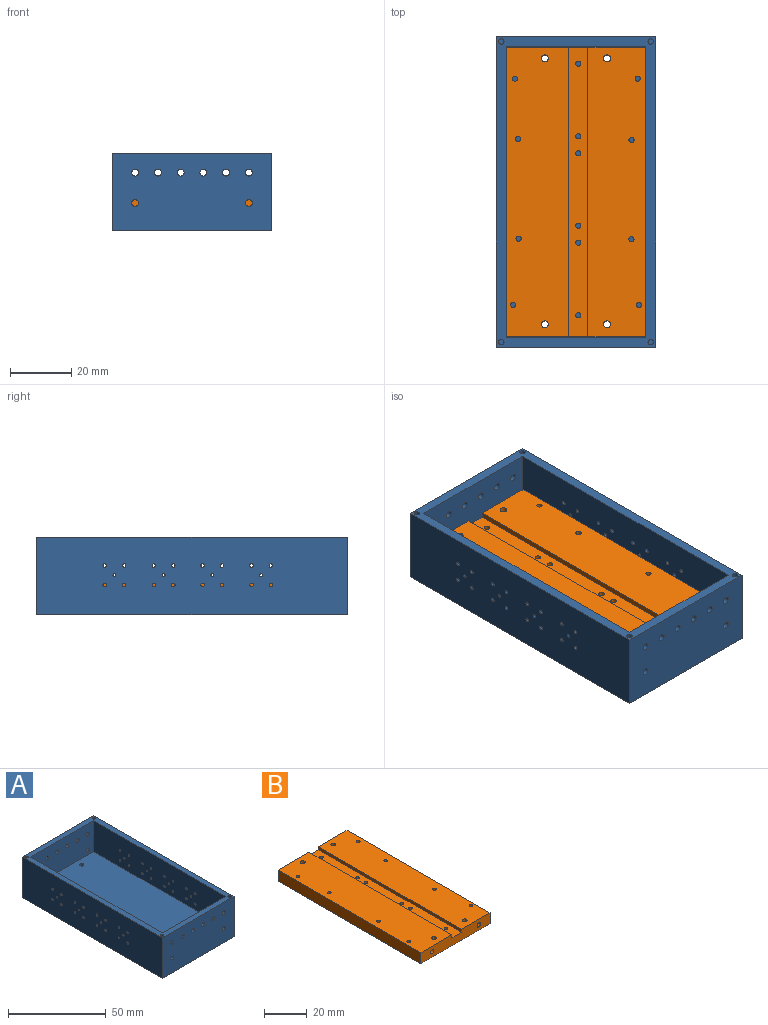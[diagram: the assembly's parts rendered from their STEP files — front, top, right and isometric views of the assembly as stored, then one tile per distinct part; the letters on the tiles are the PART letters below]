
ASSEMBLY  parts=2 mates=1
PART A: 79 faces, bbox 52.1x101.6x25.4 mm
  f0: plane 95.3x45.77mm, normal (0,0,1), area 4345.9mm2, adj f3,f5,f9,f10,f75,f76,f77,f78
  f1: plane 101.6x52.07mm, normal (0,0,-1), area 5274.3mm2, adj f2,f4,f7,f8,f75,f76,f77,f78
  f2: plane 52.07x25.4mm, normal (0,1,0), area 1290.5mm2, adj f1,f6,f7,f8,f11,f12,f13,f14
  f3: plane 45.77x19.46mm, normal (0,-1,0), area 858.4mm2, adj f0,f6,f9,f10,f11,f12,f13,f14
  f4: plane 52.07x25.4mm, normal (0,-1,0), area 1290.5mm2, adj f1,f6,f7,f8,f17,f18,f19,f20
  f5: plane 45.77x19.46mm, normal (0,1,0), area 858.4mm2, adj f0,f6,f9,f10,f17,f18,f19,f20
  f6: plane 101.6x52.07mm, normal (0,0,1), area 918.4mm2, adj f2,f3,f4,f5,f7,f8,f9,f10
  f7: plane 101.6x25.4mm, normal (-1,0,0), area 2560mm2, adj f1,f2,f4,f6,f43,f44,f45,f46
  f8: plane 101.6x25.4mm, normal (1,0,0), area 2560mm2, adj f1,f2,f4,f6,f23,f24,f25,f26
  f9: plane 95.3x19.46mm, normal (1,0,0), area 1833.6mm2, adj f0,f3,f5,f6,f43,f44,f45,f46
  f10: plane 95.3x19.46mm, normal (-1,0,0), area 1833.6mm2, adj f0,f3,f5,f6,f23,f24,f25,f26
  f11: cylinder r=1.13mm len=3.15mm, axis (0,1,0), area 22.4mm2, adj f2,f3
  f12: cylinder r=1.13mm len=3.15mm, axis (0,1,0), area 22.4mm2, adj f2,f3
  f13: cylinder r=1.13mm len=3.15mm, axis (0,1,0), area 22.4mm2, adj f2,f3
  f14: cylinder r=1.13mm len=3.15mm, axis (0,1,0), area 22.4mm2, adj f2,f3
  f15: cylinder r=1.13mm len=3.15mm, axis (0,1,0), area 22.4mm2, adj f2,f3
  f16: cylinder r=1.13mm len=3.15mm, axis (0,1,0), area 22.4mm2, adj f2,f3
  f17: cylinder r=1.13mm len=3.15mm, axis (0,-1,0), area 22.4mm2, adj f4,f5
  f18: cylinder r=1.13mm len=3.15mm, axis (0,-1,0), area 22.4mm2, adj f4,f5
  f19: cylinder r=1.13mm len=3.15mm, axis (0,-1,0), area 22.4mm2, adj f4,f5
  f20: cylinder r=1.13mm len=3.15mm, axis (0,-1,0), area 22.4mm2, adj f4,f5
  f21: cylinder r=1.13mm len=3.15mm, axis (0,-1,0), area 22.4mm2, adj f4,f5
  f22: cylinder r=1.13mm len=3.15mm, axis (0,-1,0), area 22.4mm2, adj f4,f5
  f23: cylinder r=0.59mm len=3.15mm, axis (1,0,0), area 11.7mm2, adj f8,f10
  f24: cylinder r=0.5mm len=3.15mm, axis (1,0,0), area 9.8mm2, adj f8,f10
  f25: cylinder r=0.59mm len=3.15mm, axis (1,0,0), area 11.7mm2, adj f8,f10
  f26: cylinder r=0.59mm len=3.15mm, axis (1,0,0), area 11.7mm2, adj f8,f10
  f27: cylinder r=0.59mm len=3.15mm, axis (1,0,0), area 11.7mm2, adj f8,f10
  f28: cylinder r=0.5mm len=3.15mm, axis (1,0,0), area 9.8mm2, adj f8,f10
  f29: cylinder r=0.59mm len=3.15mm, axis (1,0,0), area 11.7mm2, adj f8,f10
  f30: cylinder r=0.59mm len=3.15mm, axis (1,0,0), area 11.7mm2, adj f8,f10
  f31: cylinder r=0.59mm len=3.15mm, axis (1,0,0), area 11.7mm2, adj f8,f10
  f32: cylinder r=0.59mm len=3.15mm, axis (1,0,0), area 11.7mm2, adj f8,f10
  f33: cylinder r=0.59mm len=3.15mm, axis (1,0,0), area 11.7mm2, adj f8,f10
  f34: cylinder r=0.59mm len=3.15mm, axis (1,0,0), area 11.7mm2, adj f8,f10
  f35: cylinder r=0.59mm len=3.15mm, axis (1,0,0), area 11.7mm2, adj f8,f10
  f36: cylinder r=0.59mm len=3.15mm, axis (1,0,0), area 11.7mm2, adj f8,f10
  f37: cylinder r=0.5mm len=3.15mm, axis (1,0,0), area 9.8mm2, adj f8,f10
  f38: cylinder r=0.59mm len=3.15mm, axis (1,0,0), area 11.7mm2, adj f8,f10
  f39: cylinder r=0.5mm len=3.15mm, axis (1,0,0), area 9.8mm2, adj f8,f10
  f40: cylinder r=0.59mm len=3.15mm, axis (1,0,0), area 11.7mm2, adj f8,f10
  f41: cylinder r=0.59mm len=3.15mm, axis (1,0,0), area 11.7mm2, adj f8,f10
  f42: cylinder r=0.59mm len=3.15mm, axis (1,0,0), area 11.7mm2, adj f8,f10
  f43: cylinder r=0.59mm len=3.15mm, axis (-1,0,0), area 11.7mm2, adj f7,f9
  f44: cylinder r=0.5mm len=3.15mm, axis (-1,0,0), area 9.8mm2, adj f7,f9
  f45: cylinder r=0.59mm len=3.15mm, axis (-1,0,0), area 11.7mm2, adj f7,f9
  f46: cylinder r=0.59mm len=3.15mm, axis (-1,0,0), area 11.7mm2, adj f7,f9
  f47: cylinder r=0.59mm len=3.15mm, axis (-1,0,0), area 11.7mm2, adj f7,f9
  f48: cylinder r=0.5mm len=3.15mm, axis (-1,0,0), area 9.8mm2, adj f7,f9
  f49: cylinder r=0.59mm len=3.15mm, axis (-1,0,0), area 11.7mm2, adj f7,f9
  f50: cylinder r=0.59mm len=3.15mm, axis (-1,0,0), area 11.7mm2, adj f7,f9
  f51: cylinder r=0.59mm len=3.15mm, axis (-1,0,0), area 11.7mm2, adj f7,f9
  f52: cylinder r=0.59mm len=3.15mm, axis (-1,0,0), area 11.7mm2, adj f7,f9
  f53: cylinder r=0.59mm len=3.15mm, axis (-1,0,0), area 11.7mm2, adj f7,f9
  f54: cylinder r=0.59mm len=3.15mm, axis (-1,0,0), area 11.7mm2, adj f7,f9
  f55: cylinder r=0.59mm len=3.15mm, axis (-1,0,0), area 11.7mm2, adj f7,f9
  f56: cylinder r=0.59mm len=3.15mm, axis (-1,0,0), area 11.7mm2, adj f7,f9
  f57: cylinder r=0.5mm len=3.15mm, axis (-1,0,0), area 9.8mm2, adj f7,f9
  f58: cylinder r=0.59mm len=3.15mm, axis (-1,0,0), area 11.7mm2, adj f7,f9
  f59: cylinder r=0.5mm len=3.15mm, axis (-1,0,0), area 9.8mm2, adj f7,f9
  f60: cylinder r=0.59mm len=3.15mm, axis (-1,0,0), area 11.7mm2, adj f7,f9
  f61: cylinder r=0.59mm len=3.15mm, axis (-1,0,0), area 11.7mm2, adj f7,f9
  f62: cylinder r=0.59mm len=3.15mm, axis (-1,0,0), area 11.7mm2, adj f7,f9
  f63: cylinder r=0.89mm len=6.35mm, axis (0,0,1), area 35.5mm2, adj f6,f64
  f64: plane 1.78x1.78mm, normal (0,0,1), area 2.5mm2, adj f63
  f65: cylinder r=0.89mm len=6.35mm, axis (0,0,1), area 35.5mm2, adj f6,f66
  f66: plane 1.78x1.78mm, normal (0,0,1), area 2.5mm2, adj f65
  f67: cylinder r=0.89mm len=6.35mm, axis (0,0,1), area 35.5mm2, adj f6,f68
  f68: plane 1.78x1.78mm, normal (0,0,1), area 2.5mm2, adj f67
  f69: cylinder r=0.89mm len=6.35mm, axis (0,0,1), area 35.5mm2, adj f6,f70
  f70: plane 1.78x1.78mm, normal (0,0,1), area 2.5mm2, adj f69
  f71: cylinder r=1.13mm len=3.15mm, axis (0,-1,0), area 22.4mm2, adj f4,f5
  f72: cylinder r=1.13mm len=3.15mm, axis (0,-1,0), area 22.4mm2, adj f4,f5
  f73: cylinder r=1.13mm len=3.15mm, axis (0,1,0), area 22.4mm2, adj f2,f3
  f74: cylinder r=1.13mm len=3.15mm, axis (0,1,0), area 22.4mm2, adj f2,f3
  f75: cylinder r=1.13mm len=5.94mm, axis (0,0,1), area 42.2mm2, adj f0,f1
  f76: cylinder r=1.13mm len=5.94mm, axis (0,0,1), area 42.2mm2, adj f0,f1
  f77: cylinder r=1.13mm len=5.94mm, axis (0,0,1), area 42.2mm2, adj f0,f1
  f78: cylinder r=1.13mm len=5.94mm, axis (0,0,1), area 42.2mm2, adj f0,f1
PART B: 36 faces, bbox 45.7x94.7x6.4 mm
  f0: plane 45.72x6.35mm, normal (0,-1,0), area 272mm2, adj f2,f3,f4,f5,f6,f7,f8,f9
  f1: plane 45.72x6.35mm, normal (0,1,0), area 272mm2, adj f2,f3,f4,f5,f6,f7,f8,f9
  f2: plane 94.74x18.97mm, normal (0,0,1), area 1780.3mm2, adj f0,f1,f5,f8,f16,f17,f18,f19
  f3: plane 94.74x45.72mm, normal (0,0,-1), area 4283.9mm2, adj f0,f1,f4,f5,f10,f11,f12,f13
  f4: plane 94.74x6.35mm, normal (-1,0,0), area 601.6mm2, adj f0,f1,f3,f6
  f5: plane 94.74x6.35mm, normal (1,0,0), area 601.6mm2, adj f0,f1,f2,f3
  f6: plane 94.74x20.5mm, normal (0,0,1), area 1925.2mm2, adj f0,f1,f4,f7,f10,f11,f12,f13
  f7: plane 94.74x1.65mm, normal (1,0,0), area 156.3mm2, adj f0,f1,f6,f9
  f8: plane 94.74x1.65mm, normal (-1,0,0), area 156.3mm2, adj f0,f1,f2,f9
  f9: plane 94.74x6.25mm, normal (0,0,1), area 578.3mm2, adj f0,f1,f7,f8,f30,f31,f32,f33
  f10: cylinder r=0.85mm len=6.35mm, axis (0,0,1), area 33.8mm2, adj f3,f6
  f11: cylinder r=1.13mm len=6.35mm, axis (0,0,1), area 45.1mm2, adj f3,f6
  f12: cylinder r=1.13mm len=6.35mm, axis (0,0,1), area 45.1mm2, adj f3,f6
  f13: cylinder r=0.85mm len=6.35mm, axis (0,0,1), area 33.8mm2, adj f3,f6
  f14: cylinder r=0.85mm len=6.35mm, axis (0,0,1), area 33.8mm2, adj f3,f6
  f15: cylinder r=0.85mm len=6.35mm, axis (0,0,1), area 33.8mm2, adj f3,f6
  f16: cylinder r=1.13mm len=6.35mm, axis (0,0,1), area 45.1mm2, adj f2,f3
  f17: cylinder r=0.85mm len=6.35mm, axis (0,0,1), area 33.8mm2, adj f2,f3
  f18: cylinder r=0.85mm len=6.35mm, axis (0,0,1), area 33.8mm2, adj f2,f3
  f19: cylinder r=0.85mm len=6.35mm, axis (0,0,1), area 33.8mm2, adj f2,f3
  f20: cylinder r=1.13mm len=6.35mm, axis (0,0,1), area 45.1mm2, adj f2,f3
  f21: cylinder r=0.85mm len=6.35mm, axis (0,0,1), area 33.8mm2, adj f2,f3
  f22: cylinder r=1.13mm len=6.35mm, axis (0,1,0), area 45.1mm2, adj f1,f23
  f23: plane 2.26x2.26mm, normal (0,1,0), area 4mm2, adj f22
  f24: cylinder r=1.13mm len=6.35mm, axis (0,1,0), area 45.1mm2, adj f1,f25
  f25: plane 2.26x2.26mm, normal (0,1,0), area 4mm2, adj f24
  f26: cylinder r=1.13mm len=6.35mm, axis (0,-1,0), area 45.1mm2, adj f0,f27
  f27: plane 2.26x2.26mm, normal (0,-1,0), area 4mm2, adj f26
  f28: cylinder r=1.13mm len=6.35mm, axis (0,-1,0), area 45.1mm2, adj f0,f29
  f29: plane 2.26x2.26mm, normal (0,-1,0), area 4mm2, adj f28
  f30: cylinder r=0.85mm len=4.7mm, axis (0,0,1), area 25.1mm2, adj f3,f9
  f31: cylinder r=0.85mm len=4.7mm, axis (0,0,1), area 25.1mm2, adj f3,f9
  f32: cylinder r=0.85mm len=4.7mm, axis (0,0,1), area 25.1mm2, adj f3,f9
  f33: cylinder r=0.85mm len=4.7mm, axis (0,0,1), area 25.1mm2, adj f3,f9
  f34: cylinder r=0.85mm len=4.7mm, axis (0,0,1), area 25.1mm2, adj f3,f9
  f35: cylinder r=0.85mm len=4.7mm, axis (0,0,1), area 25.1mm2, adj f3,f9
PLACE A t=(-174.64,116.22,14.8)mm
PLACE B t=(-174.64,116.21,27.09)mm
MATE revolute B.f11 <-> A.f77  axis (0,0,-1) through (-158.76,123.72,20.74)mm
